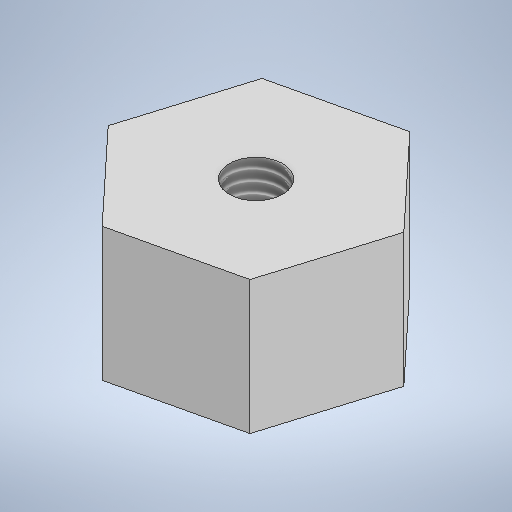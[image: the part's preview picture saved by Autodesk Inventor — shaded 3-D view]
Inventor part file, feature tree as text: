
AUTODESK INVENTOR PART (.ipt)
format: ipt  version: 2025.2 (Build 292293000, 293)  size: 205,312 bytes
history: native  units: mm
features: extrude x2, sketch x2, other x1, thread x1
ambient origin geometry x8: Origin, YZ Plane, XZ Plane, XY Plane, X Axis, Y Axis, Z Axis, Center Point
bodies: Body1 (feature_tree)
feature tree (6):
  other  "Bryła1"
  extrude  "Wyciągnięcie proste1"  Depth=4.0mm
  extrude  "Wyciągnięcie proste2"  Depth=4.5mm
  thread  "Gwint1"
  sketch  "Szkic1"
  sketch  "Szkic2"
